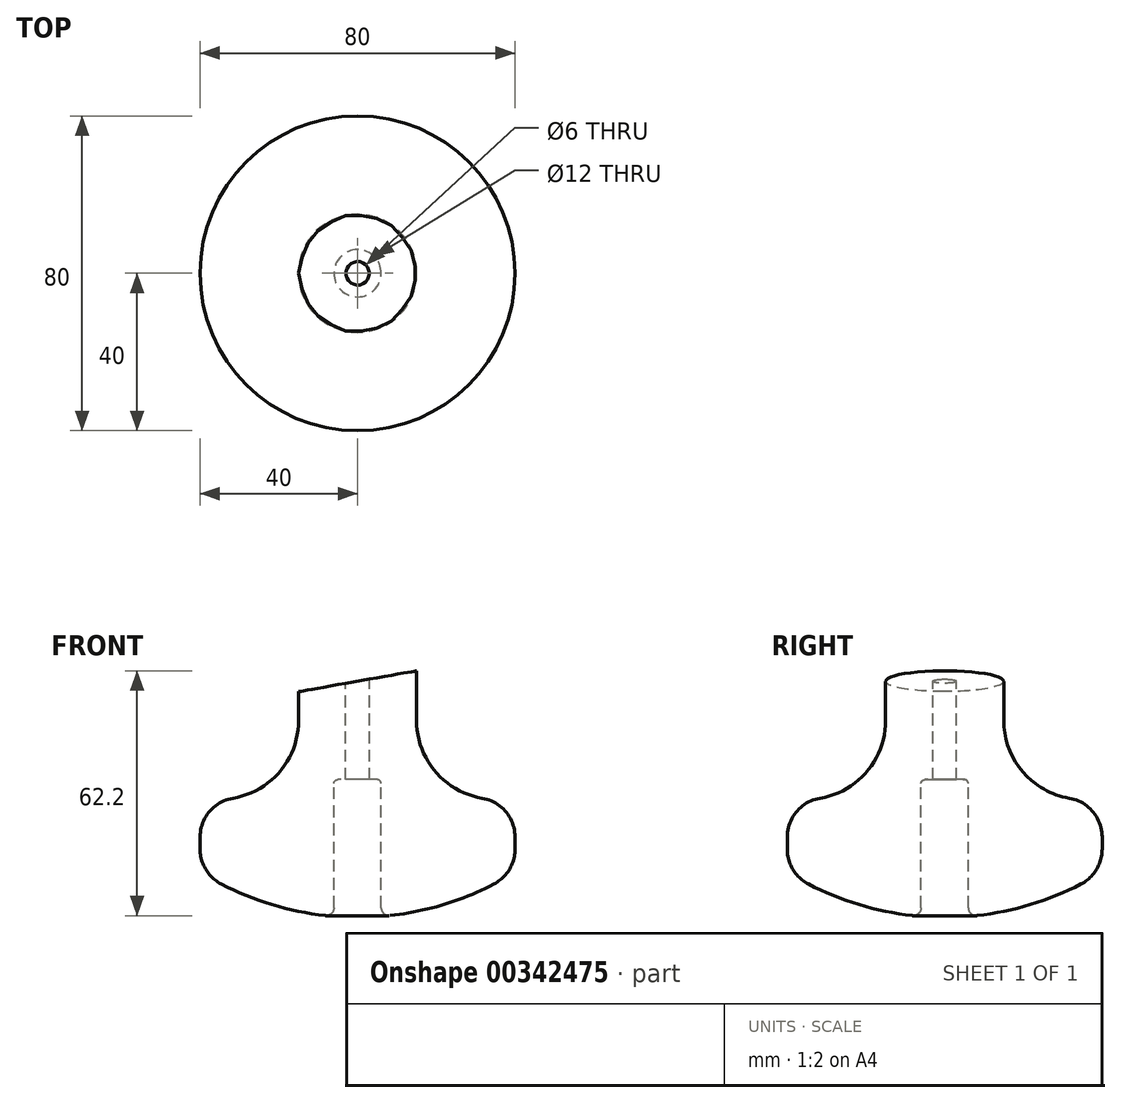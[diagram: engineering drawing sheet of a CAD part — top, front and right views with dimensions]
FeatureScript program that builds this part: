
annotation { "Feature Type Name" : "Feature", "Feature Type Description" : "" }
export const myFeature = defineFeature(function(context is Context, id is Id, definition is map)
    precondition{}
    {
        {
            var Q0;
            Q0=qCreatedBy(makeId("Front.planeOp"),FACE);
            var sketch = newSketch(context, id + "F0", { "sketchPlane" : qUnion([Q0])});
            skLineSegment(sketch, "E0", {"start": v(0, -60) * mm, "end": v(0, 0) * mm});
            skLineSegment(sketch, "E1", {"start": v(0, 0) * mm, "end": v(15, 0) * mm});
            skLineSegment(sketch, "E2", {"start": v(15, 0) * mm, "end": v(15, -30) * mm});
            skLineSegment(sketch, "E3", {"start": v(15, -30) * mm, "end": v(40, -30) * mm});
            skLineSegment(sketch, "E4", {"start": v(40, -30) * mm, "end": v(40, -48.44) * mm});
            skCircle(sketch, "E5", {"center": v(0, 15) * mm, "radius": 75 * mm});
            skLineSegment(sketch, "E6", {"start": v(15, 0) * mm, "end": v(15, 5) * mm});
            skLineSegment(sketch, "E7", {"start": v(15, 5) * mm, "end": v(0, 5) * mm});
            skLineSegment(sketch, "E8", {"start": v(0, 5) * mm, "end": v(0, 0) * mm});
            skSolve(sketch);
        }
        {
            var Q0;
            {var subQ0=sQuery(id+"F0.wireOp",EDGE,"E0");Q0=makeQuery(id+"F0.imprint","IMPRINT",FACE,{"disambiguationData":[TD([[makeQuery(id+"F0.imprint","IMPRINT",EDGE,{"derivedFrom":subQ0}),-1.0]])]});}
            var Q1;
            Q1=makeQuery(id+"F0.imprint","IMPRINT",FACE,{"disambiguationData":[TD([[makeQuery(id+"F0.imprint","IMPRINT",EDGE,{"derivedFrom":sQuery(id+"F0.wireOp",EDGE,"E1")}),1.0]])]});
            var Q2;
            Q2=sQuery(id+"F0.wireOp",EDGE,"E0");
            revolve(context, id + "F1", {"entities" : qUnion([Q0, Q1]), "axis" : qUnion([Q2]), "revolveType" : RevolveType.FULL});
        }
        {
            var Q0;
            Q0=makeQuery(id+"F1.opRevolve","SWEPT_EDGE",EDGE,{"disambiguationData":[OSD([sQuery(id+"F0.wireOp",EDGE,"E2"),sQuery(id+"F0.wireOp",EDGE,"E3")])]});
            fillet(context, id + "F2", {"entities" : qUnion([Q0]), "radius" : 20 * mm, "tangentPropagation" : true, "allowEdgeOverflow" : false});
        }
        {
            var Q0;
            Q0=makeQuery(id+"F1.opRevolve","SWEPT_EDGE",EDGE,{"disambiguationData":[OSD([sQuery(id+"F0.wireOp",EDGE,"E4"),sQuery(id+"F0.wireOp",EDGE,"E5")])]});
            var Q1;
            Q1=makeQuery(id+"F1.opRevolve","SWEPT_EDGE",EDGE,{"disambiguationData":[OSD([sQuery(id+"F0.wireOp",EDGE,"E3"),sQuery(id+"F0.wireOp",EDGE,"E4")])]});
            fillet(context, id + "F3", {"entities" : qUnion([Q0, Q1]), "radius" : 10 * mm, "tangentPropagation" : true, "allowEdgeOverflow" : false});
        }
        {
            var Q0;
            Q0=qCreatedBy(makeId("Top.planeOp"),FACE);
            var sketch = newSketch(context, id + "F4", { "sketchPlane" : qUnion([Q0])});
            skCircle(sketch, "E9", {"center": v(0, 0) * mm, "radius": 3 * mm});
            skSolve(sketch);
        }
        {
            var Q0;
            Q0=makeQuery(id+"F4.imprint","IMPRINT",FACE,{"disambiguationData":[TD([[makeQuery(id+"F4.imprint","IMPRINT",EDGE,{"derivedFrom":sQuery(id+"F4.wireOp",EDGE,"E9")}),1.0]])]});
            extrude(context, id + "F5", {"entities" : qUnion([Q0]), "operationType" : NewBodyOperationType.REMOVE, "oppositeDirection" : true, "depth" : 200 * mm, "symmetric" : true});
        }
        {
            var Q0;
            Q0=qCreatedBy(makeId("Top.planeOp"),FACE);
            var sketch = newSketch(context, id + "F6", { "sketchPlane" : qUnion([Q0])});
            skCircle(sketch, "E10", {"center": v(0, 0) * mm, "radius": 6 * mm});
            skSolve(sketch);
        }
        {
            var Q0;
            Q0=makeQuery(id+"F6.imprint","IMPRINT",FACE,{"disambiguationData":[TD([[makeQuery(id+"F6.imprint","IMPRINT",EDGE,{"derivedFrom":sQuery(id+"F6.wireOp",EDGE,"E10")}),1.0]])]});
            extrude(context, id + "F7", {"entities" : qUnion([Q0]), "operationType" : NewBodyOperationType.REMOVE, "oppositeDirection" : true, "depth" : 100 * mm, "hasSecondDirection" : true, "secondDirectionOppositeDirection" : true, "secondDirectionDepth" : 25 * mm});
        }
        {
            var Q0;
            Q0=makeQuery(id+"F7.boolean.opBoolean","COPY",EDGE,{"derivedFrom":makeQuery(id+"F7.opExtrude","CAP_EDGE",EDGE,{"disambiguationData":[OSD([sQuery(id+"F6.wireOp",EDGE,"E10")])],"isStart":true})});
            fillet(context, id + "F8", {"entities" : qUnion([Q0]), "radius" : 1 * mm, "tangentPropagation" : true, "allowEdgeOverflow" : false});
        }
        {
            var Q0;
            Q0=makeQuery(id+"F7.boolean.opBoolean","INTERSECT",EDGE,{"derivedFrom":[makeQuery(id+"F1.opRevolve","SWEPT_FACE",FACE,{"disambiguationData":[OSD([sQuery(id+"F0.wireOp",EDGE,"E5")])]}),makeQuery(id+"F7.opExtrude","SWEPT_FACE",FACE,{"disambiguationData":[OSD([sQuery(id+"F6.wireOp",EDGE,"E10")])]})]});
            fillet(context, id + "F9", {"entities" : qUnion([Q0]), "radius" : 2 * mm, "tangentPropagation" : true, "allowEdgeOverflow" : false});
        }
        {
            var Q0;
            Q0=qCreatedBy(makeId("Front.planeOp"),FACE);
            var sketch = newSketch(context, id + "F10", { "sketchPlane" : qUnion([Q0])});
            skLineSegment(sketch, "E11", {"start": v(50, 8.82) * mm, "end": v(-50, -8.82) * mm});
            skLineSegment(sketch, "E12", {"start": v(-50, -8.82) * mm, "end": v(-50, 8.82) * mm});
            skLineSegment(sketch, "E13", {"start": v(-50, 8.82) * mm, "end": v(50, 8.82) * mm});
            skSolve(sketch);
        }
        {
            var Q0;
            Q0=makeQuery(id+"F10.imprint","IMPRINT",FACE,{"disambiguationData":[TD([[makeQuery(id+"F10.imprint","IMPRINT",EDGE,{"derivedFrom":sQuery(id+"F10.wireOp",EDGE,"E11")}),-1.0]])]});
            extrude(context, id + "F11", {"entities" : qUnion([Q0]), "operationType" : NewBodyOperationType.REMOVE, "oppositeDirection" : true, "depth" : 50 * mm, "symmetric" : true});
        }
    });
